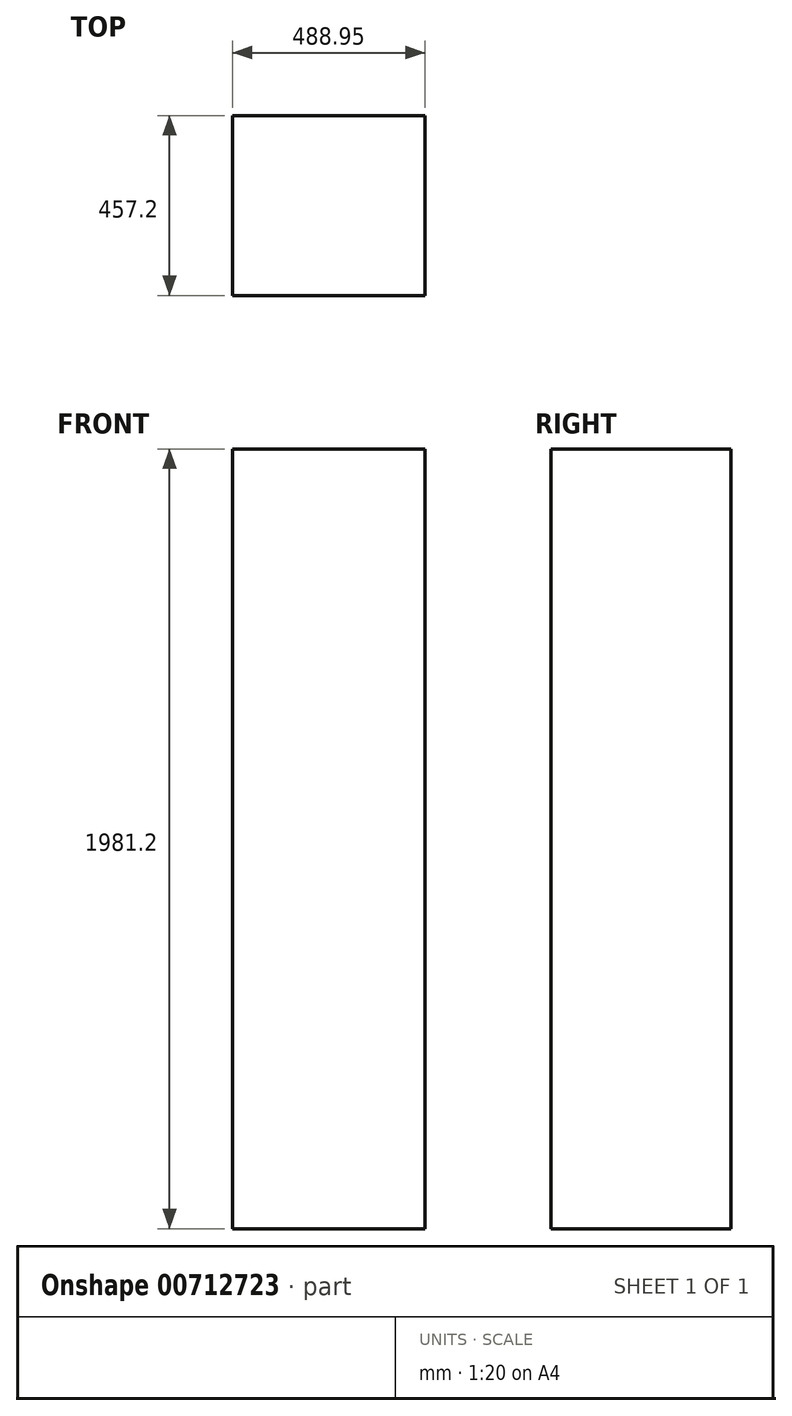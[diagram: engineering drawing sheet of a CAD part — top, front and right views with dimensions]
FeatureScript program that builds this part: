
annotation { "Feature Type Name" : "Feature", "Feature Type Description" : "" }
export const myFeature = defineFeature(function(context is Context, id is Id, definition is map)
    precondition{}
    {
        {
            var Q0;
            Q0=qCreatedBy(makeId("Top.planeOp"),FACE);
            var sketch = newSketch(context, id + "F0", { "sketchPlane" : qUnion([Q0])});
            skLineSegment(sketch, "E0.bottom", {"start": v(0, 0) * mm, "end": v(488.95, 0) * mm});
            skLineSegment(sketch, "E0.top", {"start": v(0, 457.2) * mm, "end": v(488.95, 457.2) * mm});
            skLineSegment(sketch, "E0.left", {"start": v(0, 0) * mm, "end": v(0, 457.2) * mm});
            skLineSegment(sketch, "E0.right", {"start": v(488.95, 0) * mm, "end": v(488.95, 457.2) * mm});
            skSolve(sketch);
        }
        {
            var Q0;
            Q0=qSketchRegion(id+"F0",true);
            extrude(context, id + "F1", {"entities" : qUnion([Q0]), "depth" : 1981.2 * mm, "offsetDistance" : 25.4 * mm});
        }
    });
